# Revit family: QF_BPRO_TRE 6x4_575101
name_source: partatom
category: Sonderausstattung
revit_build: Autodesk Revit 2018 (Build: 20181015_0930(x64)
units: mm (PartAtom-declared; Revit-internal decimal feet)

## family parameters
Arbeitsebenenbasiert = Nein
Beim Laden mit Abzugskörper schneiden = Nein
Bemaßung runder Anschluss = Durchmesser verwenden
Gemeinsam genutzt = Nein
Immer vertikal = Ja
Raumberechnungspunkt = Nein
Teiletyp = Normal

## types (1)
- TWE 6x4
    Artikel Nummer = 575101
    Beschreibung = TWE 6 x 4
Transportwagen
für Eurobehälter
    Beschreibung durch Hersteller analog Leistungsverzeichnislangtext = Abmessungen

Länge:			940 mm
Breite:		700 mm  
Höhe:		1585 mm


Ausführung

Der Transportwagen für Eurobehälter besteht komplett aus CNS 18/10. Die Oberfläche ist mikroliert.
Der Wagen besteht aus einer verschweißten Vierkantrohr-Konstruktion 25 x 25 mm. Rückseitig befinden sich zwei Durchschubsicherungen und stirnseitig befindet sich je eine vertikal durchlaufende Durchschubsicherung, welche dem Transportwagen zusätzliche Stabilität verleihen.
Zwei fest eingeschweißte, geschlossene Edelstahlborde, davon eins als Grundbord, das zweite im Abstand von 724 mm darüber als Zwischenbord, dienen zur Aufnahme von je 6 Eurobehältern mit dem Maß 600 × 400 mm. 
Zwei am Korpus angebrachte Schiebegriffe ermöglichen ein einfaches Manövrieren des Wagens.

Der Wagen ist fahrbar mittels stahlverzinkter Rollen (2 Bock- und 2 Lenkrollen mit Feststeller, Rollendurchmesser 160 mm). Massive Stoßecken aus Kunststoff (Polyamid) an allen vier Ecken schützen vor Beschädigung.


Optionen

•	Zwei schwenkbare frontseitige Durchschubsicherungen aus 15 x 15 mm starkem Edelstahl 


Technische Daten

Werkstoff:		CNS 18/10
Gewicht:		50 kg 
Gesamttragfähigkeit:	350 kg
Kapazität:		12 Eurobehälter 600 x 400 mm



Fabrikat

Hersteller:			B.PRO
Modell:	TRE 6 x 4
Best.Nr.	575 101
    CE Kennzeichnung = Ja
    Gerätegewicht Netto = 50.00 kg
    Großküchengerätezuordnung = Ja
    Hersteller = B.PRO GmbH
    Höhe = 1585 mm
    Internetadresse Gerätehersteller = https://www.bpro-solutions.com
    Kosten = 1584.4 $
    Länge Gerätebreite = 940 mm
    Material = QF_Metal-Stainless-Steel_general
    Material Griff = QF_Metal-Aluminium_glossy
    Material Rollen = QF_Metal-Stainless-Steel_general
    Material Stoßschutz = QF_Plastic-Dark_Grey-Matt
    Modell = TWE 6x4
    Tiefe = 700 mm
    Typenkommentare = Transportwagen für Eurobehälter
    URL = https://www.bpro-solutions.com
    Zubehör = Ja
